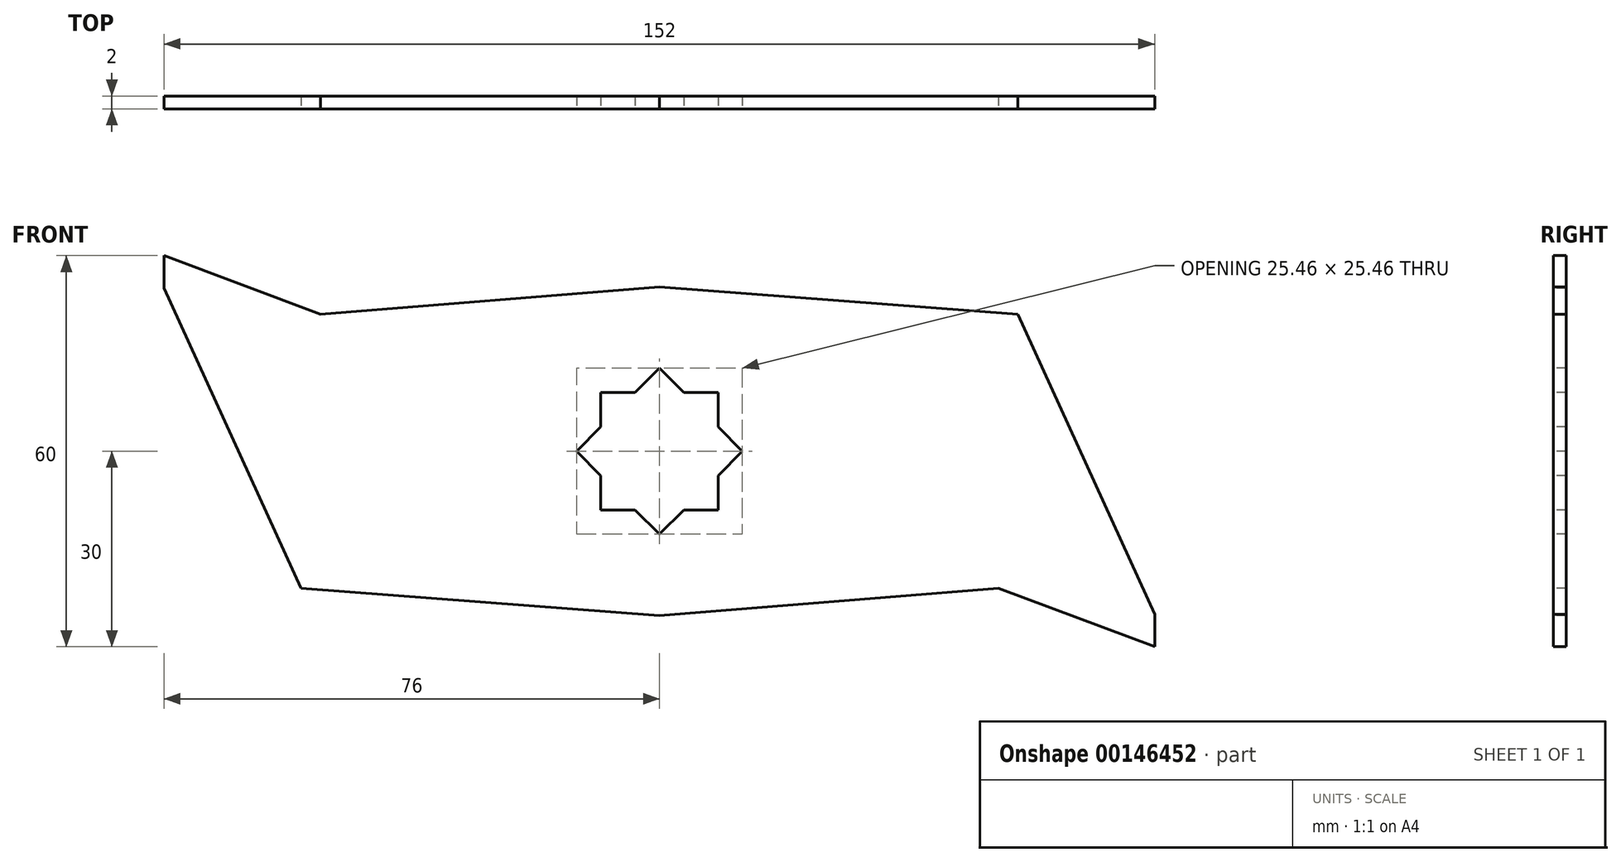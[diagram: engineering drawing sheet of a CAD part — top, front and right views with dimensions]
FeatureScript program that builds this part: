
annotation { "Feature Type Name" : "Feature", "Feature Type Description" : "" }
export const myFeature = defineFeature(function(context is Context, id is Id, definition is map)
    precondition{}
    {
        {
            var Q0;
            Q0=qCreatedBy(makeId("Front.planeOp"),FACE);
            var sketch = newSketch(context, id + "F0", { "sketchPlane" : qUnion([Q0])});
            skLineSegment(sketch, "E0.bottom", {"start": v(9, 9) * mm, "end": v(3.73, 9) * mm});
            skLineSegment(sketch, "E0.left", {"start": v(9, 9) * mm, "end": v(9, 3.73) * mm});
            skLineSegment(sketch, "E0.right", {"start": v(-9, 9) * mm, "end": v(-9, 3.73) * mm});
            skPoint(sketch, "E0.middle", {"position": v(0, 0) * mm});
            skLineSegment(sketch, "E1.0", {"start": v(0, 12.73) * mm, "end": v(3.73, 9) * mm});
            skLineSegment(sketch, "E1.1", {"start": v(12.73, 0) * mm, "end": v(9, -3.73) * mm});
            skLineSegment(sketch, "E1.2", {"start": v(0, -12.73) * mm, "end": v(-3.73, -9) * mm});
            skLineSegment(sketch, "E1.3", {"start": v(-12.73, 0) * mm, "end": v(-9, 3.73) * mm});
            skPoint(sketch, "E1.0.midPoint", {"position": v(6.36, 6.36) * mm});
            skPoint(sketch, "E2", {"position": v(0, 25.23) * mm});
            skPoint(sketch, "E3", {"position": v(0, -25.23) * mm});
            skPoint(sketch, "E4", {"position": v(-52, 21) * mm});
            skLineSegment(sketch, "E5", {"start": v(0, 25.23) * mm, "end": v(-52, 21) * mm});
            skPoint(sketch, "E6", {"position": v(-76, 30) * mm});
            skLineSegment(sketch, "E7", {"start": v(-52, 21) * mm, "end": v(-76, 30) * mm});
            skPoint(sketch, "E8", {"position": v(-76, 25) * mm});
            skPoint(sketch, "E9", {"position": v(-55, -21) * mm});
            skLineSegment(sketch, "E10", {"start": v(-76, 30) * mm, "end": v(-76, 25) * mm});
            skLineSegment(sketch, "E11", {"start": v(-76, 25) * mm, "end": v(-55, -21) * mm});
            skLineSegment(sketch, "E12", {"start": v(-55, -21) * mm, "end": v(0, -25.23) * mm});
            skLineSegment(sketch, "E13", {"start": v(0, 12.73) * mm, "end": v(0, -12.73) * mm});
            skPoint(sketch, "E14.MirrorP", {"position": v(76, 30) * mm});
            skPoint(sketch, "E15.MirrorP", {"position": v(55, -21) * mm});
            skLineSegment(sketch, "E16.MirrorCS", {"start": v(0, -25.23) * mm, "end": v(52, -21) * mm});
            skLineSegment(sketch, "E17.MirrorCS", {"start": v(52, -21) * mm, "end": v(76, -30) * mm});
            skLineSegment(sketch, "E18.MirrorCS", {"start": v(76, -30) * mm, "end": v(76, -25) * mm});
            skLineSegment(sketch, "E19.MirrorCS", {"start": v(76, -25) * mm, "end": v(55, 21) * mm});
            skLineSegment(sketch, "E20.MirrorCS", {"start": v(55, 21) * mm, "end": v(0, 25.23) * mm});
            skLineSegment(sketch, "E21.trimOffspring", {"start": v(-3.73, 9) * mm, "end": v(0, 12.73) * mm});
            skLineSegment(sketch, "E22.trimOffspring", {"start": v(-9, -3.73) * mm, "end": v(-9, -9) * mm});
            skLineSegment(sketch, "E23.trimOffspring", {"start": v(-3.73, -9) * mm, "end": v(-9, -9) * mm});
            skLineSegment(sketch, "E24.trimOffspring", {"start": v(9, 3.73) * mm, "end": v(12.73, 0) * mm});
            skLineSegment(sketch, "E25.trimOffspring", {"start": v(-3.73, 9) * mm, "end": v(-9, 9) * mm});
            skLineSegment(sketch, "E26.trimOffspring", {"start": v(9, -3.73) * mm, "end": v(9, -9) * mm});
            skLineSegment(sketch, "E27.trimOffspring", {"start": v(-9, -3.73) * mm, "end": v(-12.73, 0) * mm});
            skLineSegment(sketch, "E28", {"start": v(9, -9) * mm, "end": v(3.73, -9) * mm});
            skLineSegment(sketch, "E29.trimOffspring", {"start": v(3.73, -9) * mm, "end": v(0, -12.73) * mm});
            skSolve(sketch);
        }
        {
            var Q0;
            Q0 = qSketchRegion(id + "F0", true);
            extrude(context, id + "F1", {"entities" : qUnion([Q0]), "endBound" : BoundingType.SYMMETRIC, "oppositeDirection" : true, "depth" : 2 * mm});
        }
    });
